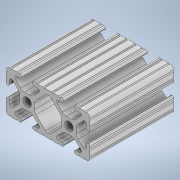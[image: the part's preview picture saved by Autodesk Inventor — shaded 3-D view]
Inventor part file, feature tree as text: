
AUTODESK INVENTOR PART (.ipt)
format: ipt  version: 2020 (Build 240168000, 168)  size: 335,872 bytes
history: native  units: in
note: dims shown in document units (in); Inventor stores cm internally (conversion verified against a paired STEP export)
features: sketch x2, extrude x1
ambient origin geometry x8: Origin, YZ Plane, XZ Plane, XY Plane, X Axis, Y Axis, Z Axis, Center Point
bodies: Solid1 (feature_tree)
feature tree (3):
  extrude  "Extrusion1"  [1 undecoded]
  sketch  "Sketch2"
  sketch  "Sketch1"  dims[d0=2.0in d1=0.0in]
note: 1 required parameter value undecoded (feature->parameter linkage not recoverable at this tier; creation-order binding heuristic only, values carry confidence <= 0.55)
